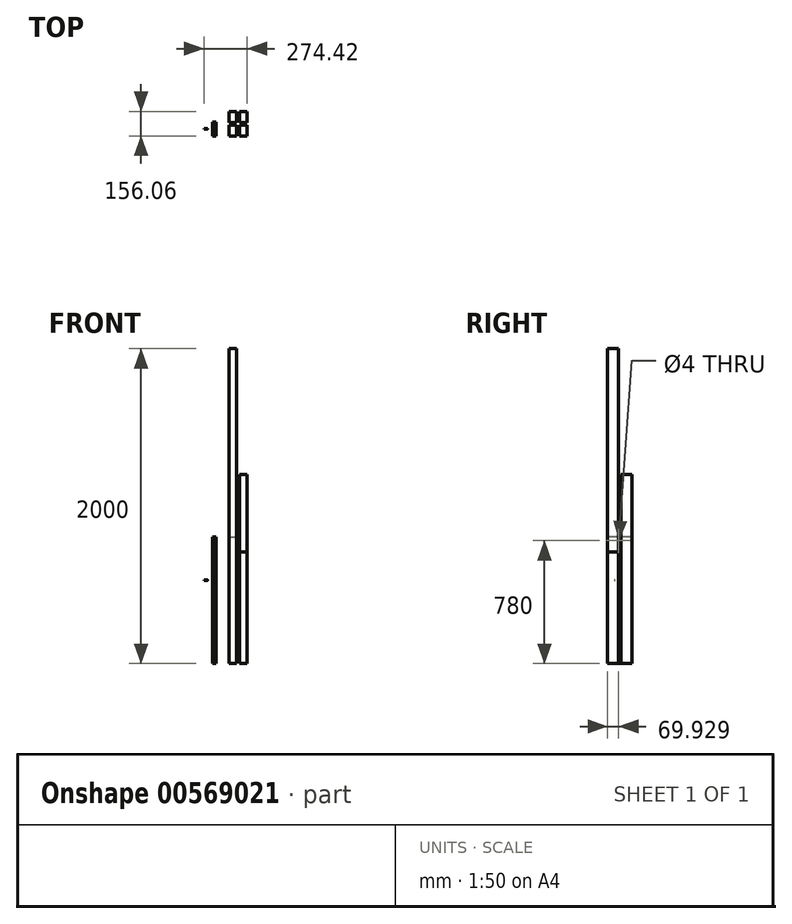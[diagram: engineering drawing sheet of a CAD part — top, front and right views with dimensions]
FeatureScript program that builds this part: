
annotation { "Feature Type Name" : "Feature", "Feature Type Description" : "" }
export const myFeature = defineFeature(function(context is Context, id is Id, definition is map)
    precondition{}
    {
        {
            var Q0;
            Q0=qCreatedBy(makeId("Top.planeOp"),FACE);
            var sketch = newSketch(context, id + "F0", { "sketchPlane" : qUnion([Q0])});
            skLineSegment(sketch, "E0.bottom", {"start": v(-40.53, 52.4) * mm, "end": v(7.47, 52.4) * mm});
            skLineSegment(sketch, "E0.top", {"start": v(-40.53, -17.6) * mm, "end": v(7.47, -17.6) * mm});
            skLineSegment(sketch, "E0.left", {"start": v(-40.53, 52.4) * mm, "end": v(-40.53, -17.6) * mm});
            skLineSegment(sketch, "E0.right", {"start": v(7.47, 52.4) * mm, "end": v(7.47, -17.6) * mm});
            skLineSegment(sketch, "E1.0.1.0", {"start": v(-40.53, 138.4) * mm, "end": v(7.47, 138.4) * mm});
            skLineSegment(sketch, "E1.0.1.1", {"start": v(-40.53, 68.4) * mm, "end": v(7.47, 68.4) * mm});
            skLineSegment(sketch, "E1.0.1.2", {"start": v(-40.53, 138.4) * mm, "end": v(-40.53, 68.4) * mm});
            skLineSegment(sketch, "E1.0.1.3", {"start": v(7.47, 138.4) * mm, "end": v(7.47, 68.4) * mm});
            skLineSegment(sketch, "E1.1.0.0", {"start": v(25.47, 52.4) * mm, "end": v(73.47, 52.4) * mm});
            skLineSegment(sketch, "E1.1.0.1", {"start": v(25.47, -17.6) * mm, "end": v(73.47, -17.6) * mm});
            skLineSegment(sketch, "E1.1.0.2", {"start": v(25.47, 52.4) * mm, "end": v(25.47, -17.6) * mm});
            skLineSegment(sketch, "E1.1.0.3", {"start": v(73.47, 52.4) * mm, "end": v(73.47, -17.6) * mm});
            skLineSegment(sketch, "E1.1.1.0", {"start": v(25.47, 138.4) * mm, "end": v(73.47, 138.4) * mm});
            skLineSegment(sketch, "E1.1.1.1", {"start": v(25.47, 68.4) * mm, "end": v(73.47, 68.4) * mm});
            skLineSegment(sketch, "E1.1.1.2", {"start": v(25.47, 138.4) * mm, "end": v(25.47, 68.4) * mm});
            skLineSegment(sketch, "E1.1.1.3", {"start": v(73.47, 138.4) * mm, "end": v(73.47, 68.4) * mm});
            skLineSegment(sketch, "E1.2.0.0", {"start": v(91.47, 52.4) * mm, "end": v(139.47, 52.4) * mm});
            skLineSegment(sketch, "E1.2.0.1", {"start": v(91.47, -17.6) * mm, "end": v(139.47, -17.6) * mm});
            skLineSegment(sketch, "E1.2.0.2", {"start": v(91.47, 52.4) * mm, "end": v(91.47, -17.6) * mm});
            skLineSegment(sketch, "E1.2.0.3", {"start": v(139.47, 52.4) * mm, "end": v(139.47, -17.6) * mm});
            skLineSegment(sketch, "E1.2.1.0", {"start": v(91.47, 138.4) * mm, "end": v(139.47, 138.4) * mm});
            skLineSegment(sketch, "E1.2.1.1", {"start": v(91.47, 68.4) * mm, "end": v(139.47, 68.4) * mm});
            skLineSegment(sketch, "E1.2.1.2", {"start": v(91.47, 138.4) * mm, "end": v(91.47, 68.4) * mm});
            skLineSegment(sketch, "E1.2.1.3", {"start": v(139.47, 138.4) * mm, "end": v(139.47, 68.4) * mm});
            skLineSegment(sketch, "E1.direction1", {"start": v(-40.53, -17.6) * mm, "end": v(25.47, -17.6) * mm, "construction": true});
            skLineSegment(sketch, "E1.direction2", {"start": v(-40.53, -17.6) * mm, "end": v(-40.53, 68.4) * mm, "construction": true});
            skSolve(sketch);
        }
        {
            var Q0;
            Q0=makeQuery(id+"F0.imprint","IMPRINT",FACE,{"disambiguationData":[TD([[makeQuery(id+"F0.imprint","IMPRINT",EDGE,{"derivedFrom":sQuery(id+"F0.wireOp",EDGE,"E0.bottom")}),-1.0]])]});
            extrude(context, id + "F1", {"entities" : qUnion([Q0]), "depth" : 2000 * mm, "offsetDistance" : 25 * mm});
        }
        {
            var Q0;
            Q0=makeQuery(id+"F0.imprint","IMPRINT",FACE,{"disambiguationData":[TD([[makeQuery(id+"F0.imprint","IMPRINT",EDGE,{"derivedFrom":sQuery(id+"F0.wireOp",EDGE,"E1.0.1.0")}),-1.0]])]});
            extrude(context, id + "F2", {"entities" : qUnion([Q0]), "depth" : (900 - 96) * mm, "offsetDistance" : 25 * mm});
        }
        {
            var Q0;
            Q0=makeQuery(id+"F0.imprint","IMPRINT",FACE,{"disambiguationData":[TD([[makeQuery(id+"F0.imprint","IMPRINT",EDGE,{"derivedFrom":sQuery(id+"F0.wireOp",EDGE,"E1.1.1.0")}),-1.0]])]});
            extrude(context, id + "F3", {"entities" : qUnion([Q0]), "depth" : 1200 * mm, "offsetDistance" : 25 * mm});
        }
        {
            var Q0;
            Q0=makeQuery(id+"F0.imprint","IMPRINT",FACE,{"disambiguationData":[TD([[makeQuery(id+"F0.imprint","IMPRINT",EDGE,{"derivedFrom":sQuery(id+"F0.wireOp",EDGE,"E1.1.0.0")}),-1.0]])]});
            extrude(context, id + "F4", {"entities" : qUnion([Q0]), "depth" : (900 - 96 - 96) * mm, "offsetDistance" : 25 * mm});
        }
        {
            var Q0;
            Q0=qCreatedBy(makeId("Top.planeOp"),FACE);
            var sketch = newSketch(context, id + "F5", { "sketchPlane" : qUnion([Q0])});
            skLineSegment(sketch, "E2.bottom", {"start": v(-144.95, 72.34) * mm, "end": v(-122.95, 72.34) * mm});
            skLineSegment(sketch, "E2.top", {"start": v(-144.95, -17.66) * mm, "end": v(-122.95, -17.66) * mm});
            skLineSegment(sketch, "E2.left", {"start": v(-144.95, 72.34) * mm, "end": v(-144.95, -17.66) * mm});
            skLineSegment(sketch, "E2.right", {"start": v(-122.95, 72.34) * mm, "end": v(-122.95, -17.66) * mm});
            skLineSegment(sketch, "E3.1.0.0", {"start": v(-200.95, 72.34) * mm, "end": v(-178.95, 72.34) * mm});
            skLineSegment(sketch, "E3.1.0.1", {"start": v(-200.95, -17.66) * mm, "end": v(-178.95, -17.66) * mm});
            skLineSegment(sketch, "E3.1.0.2", {"start": v(-200.95, 72.34) * mm, "end": v(-200.95, -17.66) * mm});
            skLineSegment(sketch, "E3.1.0.3", {"start": v(-178.95, 72.34) * mm, "end": v(-178.95, -17.66) * mm});
            skLineSegment(sketch, "E3.2.0.0", {"start": v(-256.95, 72.34) * mm, "end": v(-234.95, 72.34) * mm});
            skLineSegment(sketch, "E3.2.0.1", {"start": v(-256.95, -17.66) * mm, "end": v(-234.95, -17.66) * mm});
            skLineSegment(sketch, "E3.2.0.2", {"start": v(-256.95, 72.34) * mm, "end": v(-256.95, -17.66) * mm});
            skLineSegment(sketch, "E3.2.0.3", {"start": v(-234.95, 72.34) * mm, "end": v(-234.95, -17.66) * mm});
            skLineSegment(sketch, "E3.direction1", {"start": v(-144.95, -17.66) * mm, "end": v(-200.95, -17.66) * mm, "construction": true});
            skSolve(sketch);
        }
        {
            var Q0;
            Q0=makeQuery(id+"F5.imprint","IMPRINT",FACE,{"disambiguationData":[TD([[makeQuery(id+"F5.imprint","IMPRINT",EDGE,{"derivedFrom":sQuery(id+"F5.wireOp",EDGE,"E2.bottom")}),-1.0]])]});
            extrude(context, id + "F6", {"entities" : qUnion([Q0]), "depth" : (900 - 96) * mm, "offsetDistance" : 25 * mm});
        }
        {
            var Q0;
            Q0=makeQuery(id+"F6.opExtrude","SWEPT_FACE",FACE,{"disambiguationData":[OSD([sQuery(id+"F5.wireOp",EDGE,"E2.left")])]});
            var sketch = newSketch(context, id + "F7", { "sketchPlane" : qUnion([Q0])});
            skCircle(sketch, "E4", {"center": v(-52.27, 780) * mm, "radius": 2 * mm});
            skSolve(sketch);
        }
        {
            var Q0;
            Q0=makeQuery(id+"F7.imprint","IMPRINT",FACE,{"disambiguationData":[TD([[makeQuery(id+"F7.imprint","IMPRINT",EDGE,{"derivedFrom":sQuery(id+"F7.wireOp",EDGE,"E4")}),1.0]])]});
            extrude(context, id + "F8", {"entities" : qUnion([Q0]), "operationType" : NewBodyOperationType.REMOVE, "endBound" : BoundingType.UP_TO_NEXT, "oppositeDirection" : true, "depth" : 25 * mm, "offsetDistance" : 25 * mm});
        }
        {
            var Q0;
            Q0=makeQuery(id+"F5.imprint","IMPRINT",FACE,{"disambiguationData":[TD([[makeQuery(id+"F5.imprint","IMPRINT",EDGE,{"derivedFrom":sQuery(id+"F5.wireOp",EDGE,"E3.1.0.0")}),-1.0]])]});
            extrude(context, id + "F9", {"entities" : qUnion([Q0]), "depth" : 540 * mm, "offsetDistance" : 25 * mm});
        }
        {
            var Q0;
            Q0=makeQuery(id+"F9.opExtrude","SWEPT_FACE",FACE,{"disambiguationData":[OSD([sQuery(id+"F5.wireOp",EDGE,"E3.1.0.2")])]});
            var sketch = newSketch(context, id + "F10", { "sketchPlane" : qUnion([Q0])});
            skLineSegment(sketch, "E5", {"start": v(-72.34, 270) * mm, "end": v(50.98, 270) * mm, "construction": true});
            skCircle(sketch, "E6", {"center": v(-27.34, 11) * mm, "radius": 2 * mm});
            skPoint(sketch, "E6.centerSnap0", {"position": v(-27.34, 0) * mm});
            skCircle(sketch, "E7.MirrorC", {"center": v(-27.34, 529) * mm, "radius": 2 * mm});
            skSolve(sketch);
        }
        {
            var Q0;
            Q0=makeQuery(id+"F10.imprint","IMPRINT",FACE,{"disambiguationData":[TD([[makeQuery(id+"F10.imprint","IMPRINT",EDGE,{"derivedFrom":sQuery(id+"F10.wireOp",EDGE,"E7.MirrorC")}),-1.0]])]});
            var Q1;
            Q1=makeQuery(id+"F10.imprint","IMPRINT",FACE,{"disambiguationData":[TD([[makeQuery(id+"F10.imprint","IMPRINT",EDGE,{"derivedFrom":sQuery(id+"F10.wireOp",EDGE,"E6")}),1.0]])]});
            extrude(context, id + "F11", {"entities" : qUnion([Q0, Q1]), "operationType" : NewBodyOperationType.REMOVE, "endBound" : BoundingType.UP_TO_NEXT, "oppositeDirection" : true, "depth" : 25 * mm, "offsetDistance" : 25 * mm});
        }
    });
